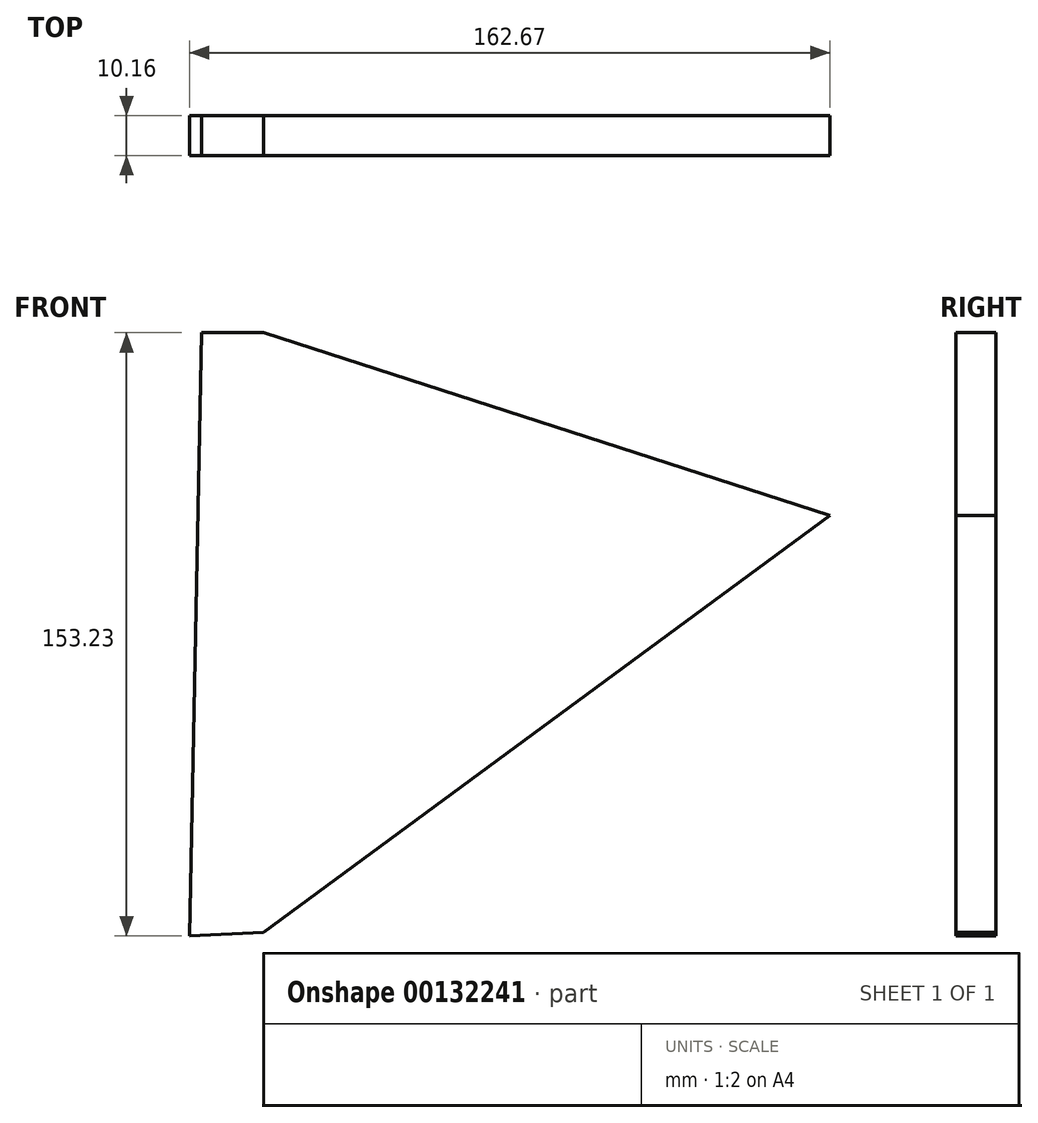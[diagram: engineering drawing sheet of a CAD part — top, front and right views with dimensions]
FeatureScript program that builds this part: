
annotation { "Feature Type Name" : "Feature", "Feature Type Description" : "" }
export const myFeature = defineFeature(function(context is Context, id is Id, definition is map)
    precondition{}
    {
        {
            var Q0;
            Q0=qCreatedBy(makeId("Front.planeOp"),FACE);
            var sketch = newSketch(context, id + "F0", { "sketchPlane" : qUnion([Q0])});
            skLineSegment(sketch, "E0", {"start": v(-66.61, 75.83) * mm, "end": v(-66.61, -76.47) * mm});
            skLineSegment(sketch, "E1", {"start": v(-66.61, 75.83) * mm, "end": v(77.31, 29.38) * mm});
            skLineSegment(sketch, "E2", {"start": v(77.31, 29.38) * mm, "end": v(-66.61, -76.47) * mm});
            skLineSegment(sketch, "E3", {"start": v(-66.61, 75.83) * mm, "end": v(-82.36, 75.83) * mm});
            skLineSegment(sketch, "E4", {"start": v(-82.36, 75.83) * mm, "end": v(-85.36, -77.4) * mm});
            skLineSegment(sketch, "E5", {"start": v(-85.36, -77.4) * mm, "end": v(-66.61, -76.47) * mm});
            skSolve(sketch);
        }
        {
            var Q0;
            Q0 = qSketchRegion(id + "F0", true);
            extrude(context, id + "F1", {"entities" : qUnion([Q0]), "depth" : 10.16 * mm});
        }
    });
